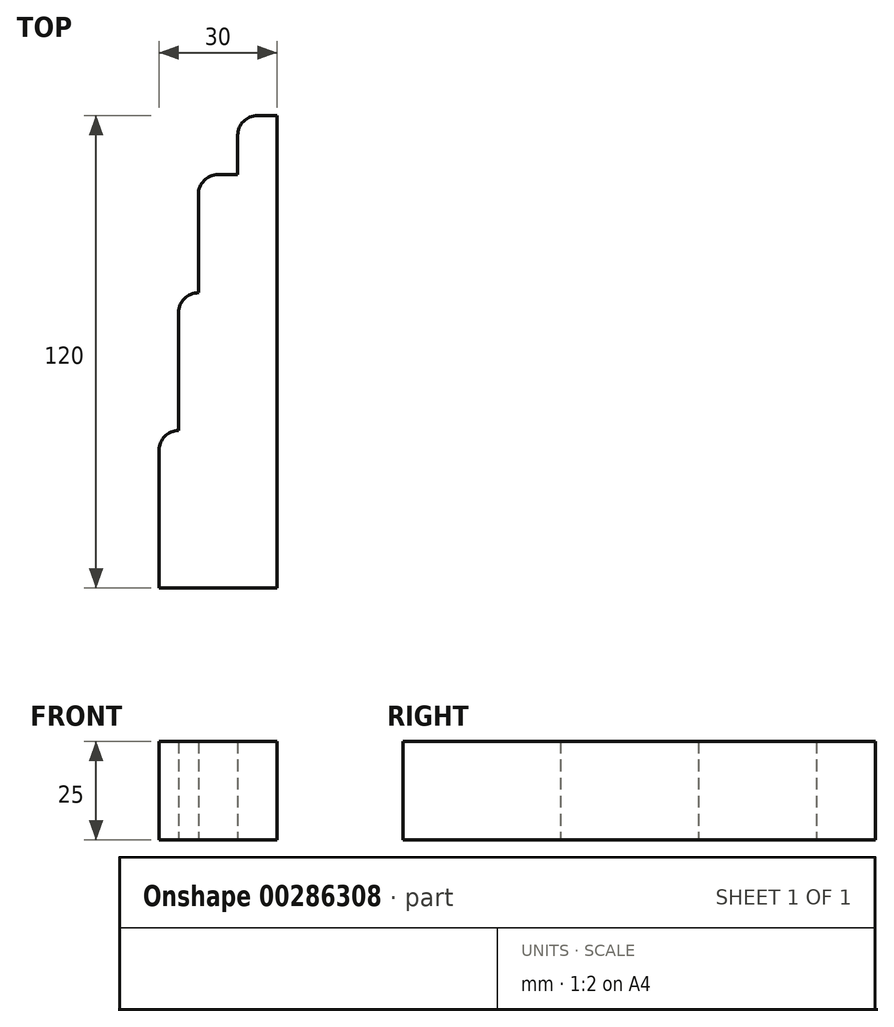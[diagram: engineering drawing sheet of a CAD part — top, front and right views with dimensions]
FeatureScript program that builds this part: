
annotation { "Feature Type Name" : "Feature", "Feature Type Description" : "" }
export const myFeature = defineFeature(function(context is Context, id is Id, definition is map)
    precondition{}
    {
        {
            var Q0;
            Q0=qCreatedBy(makeId("Top.planeOp"),FACE);
            var sketch = newSketch(context, id + "F0", { "sketchPlane" : qUnion([Q0])});
            skLineSegment(sketch, "E0", {"start": v(10, 52.12) * mm, "end": v(10, -67.88) * mm});
            skLineSegment(sketch, "E1", {"start": v(10, -67.88) * mm, "end": v(-20, -67.88) * mm});
            skLineSegment(sketch, "E2", {"start": v(-20, -67.88) * mm, "end": v(-20, -32.88) * mm});
            skLineSegment(sketch, "E3", {"start": v(-15, -27.88) * mm, "end": v(-15, -27.88) * mm});
            skLineSegment(sketch, "E4", {"start": v(-15, -27.88) * mm, "end": v(-15, 2.12) * mm});
            skLineSegment(sketch, "E5", {"start": v(-10, 7.12) * mm, "end": v(-10, 7.12) * mm});
            skLineSegment(sketch, "E6", {"start": v(-10, 7.12) * mm, "end": v(-10, 32.12) * mm});
            skLineSegment(sketch, "E7", {"start": v(-5, 37.12) * mm, "end": v(0, 37.12) * mm});
            skLineSegment(sketch, "E8", {"start": v(0, 37.12) * mm, "end": v(0, 47.12) * mm});
            skLineSegment(sketch, "E9", {"start": v(5, 52.12) * mm, "end": v(10, 52.12) * mm});
            skPoint(sketch, "E10.visualSharp", {"position": v(-20, -27.88) * mm});
            skArc(sketch, "E10.filletArc", {"start": v(-15, -27.88) * mm, "mid": v(-18.54, -29.34) * mm, "end": v(-20, -32.88) * mm});
            skPoint(sketch, "E11.visualSharp", {"position": v(-15, 7.12) * mm});
            skArc(sketch, "E11.filletArc", {"start": v(-10, 7.12) * mm, "mid": v(-13.54, 5.66) * mm, "end": v(-15, 2.12) * mm});
            skPoint(sketch, "E12.visualSharp", {"position": v(-10, 37.12) * mm});
            skArc(sketch, "E12.filletArc", {"start": v(-5, 37.12) * mm, "mid": v(-8.54, 35.66) * mm, "end": v(-10, 32.12) * mm});
            skPoint(sketch, "E13.visualSharp", {"position": v(0, 52.12) * mm});
            skArc(sketch, "E13.filletArc", {"start": v(5, 52.12) * mm, "mid": v(1.46, 50.66) * mm, "end": v(0, 47.12) * mm});
            skSolve(sketch);
        }
        {
            var Q0;
            Q0 = qSketchRegion(id + "F0", true);
            extrude(context, id + "F1", {"entities" : qUnion([Q0]), "depth" : 25 * mm});
        }
    });
